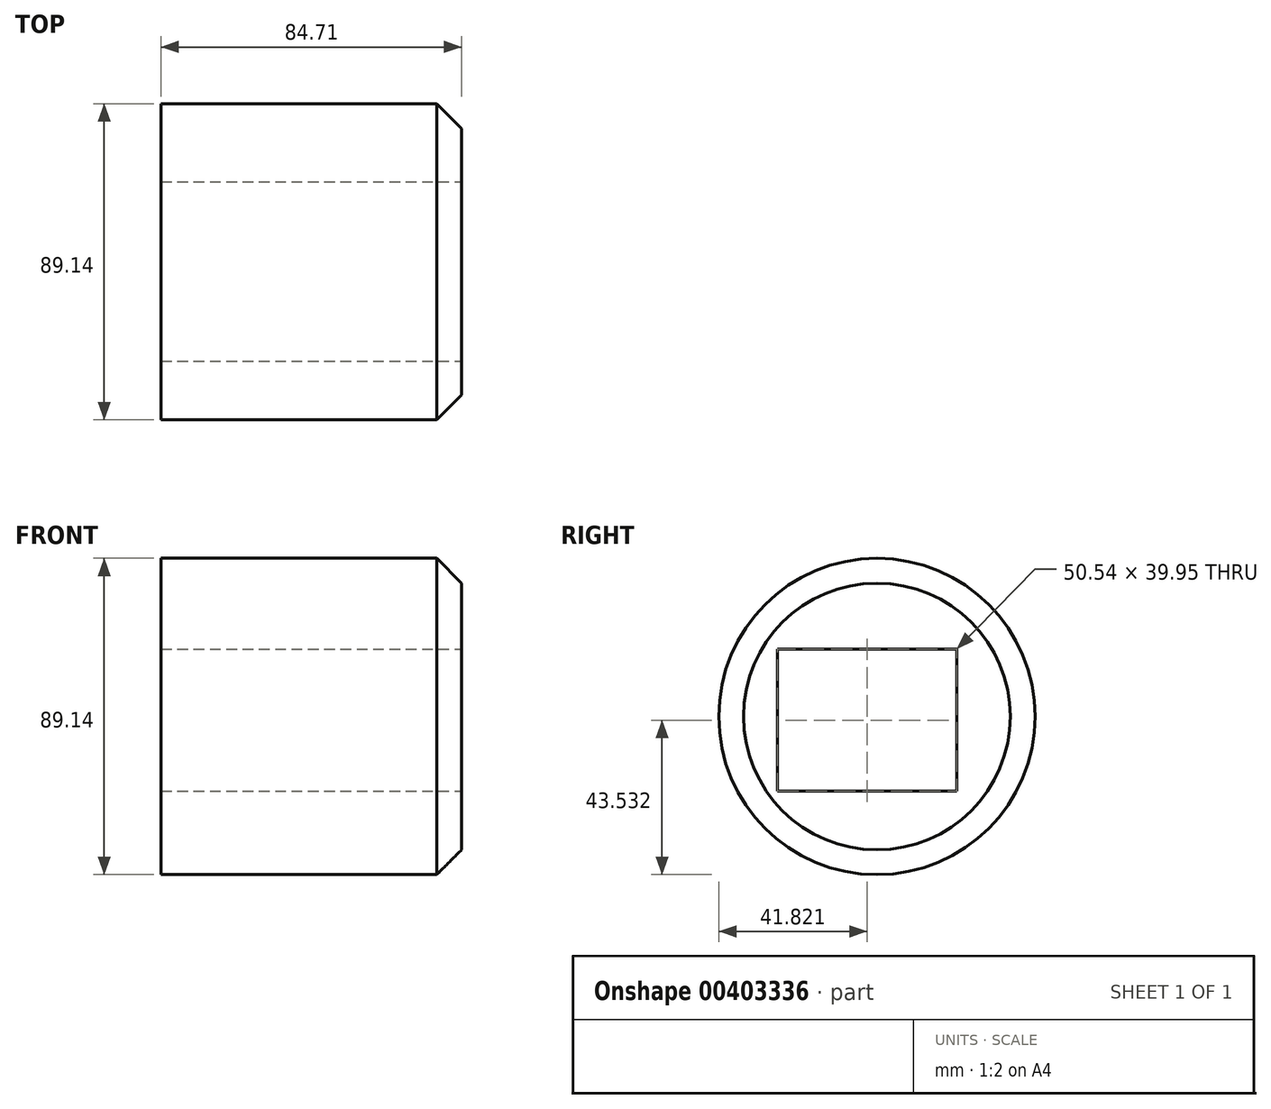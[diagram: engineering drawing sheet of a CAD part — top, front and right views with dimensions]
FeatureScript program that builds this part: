
annotation { "Feature Type Name" : "Feature", "Feature Type Description" : "" }
export const myFeature = defineFeature(function(context is Context, id is Id, definition is map)
    precondition{}
    {
        {
            var Q0;
            Q0=qCreatedBy(makeId("Right.planeOp"),FACE);
            var sketch = newSketch(context, id + "F0", { "sketchPlane" : qUnion([Q0])});
            skCircle(sketch, "E0", {"center": v(0, 0) * mm, "radius": 44.57 * mm});
            skSolve(sketch);
        }
        {
            var Q0;
            Q0=makeQuery(id+"F0.imprint","IMPRINT",FACE,{"disambiguationData":[TD([[makeQuery(id+"F0.imprint","IMPRINT",EDGE,{"derivedFrom":sQuery(id+"F0.wireOp",EDGE,"E0")}),1.0]])]});
            extrude(context, id + "F1", {"entities" : qUnion([Q0]), "depth" : 59.7 * mm});
        }
        {
            var Q0;
            Q0=makeQuery(id+"F1.opExtrude","CAP_FACE",FACE,{"disambiguationData":[OSD([sQuery(id+"F0.wireOp",EDGE,"E0")])],"isStart":false});
            extrude(context, id + "F2", {"entities" : qUnion([Q0]), "operationType" : NewBodyOperationType.ADD, "depth" : 25 * mm});
        }
        {
            var Q0;
            Q0=makeQuery(id+"F2.opExtrude","CAP_FACE",FACE,{"disambiguationData":[OSD([sQuery(id+"F0.wireOp",EDGE,"E0")])],"isStart":false});
            var sketch = newSketch(context, id + "F3", { "sketchPlane" : qUnion([Q0])});
            skLineSegment(sketch, "E1.bottom", {"start": v(22.52, 18.94) * mm, "end": v(-28.02, 18.94) * mm});
            skLineSegment(sketch, "E1.top", {"start": v(22.52, -21.01) * mm, "end": v(-28.02, -21.01) * mm});
            skLineSegment(sketch, "E1.left", {"start": v(22.52, 18.94) * mm, "end": v(22.52, -21.01) * mm});
            skLineSegment(sketch, "E1.right", {"start": v(-28.02, 18.94) * mm, "end": v(-28.02, -21.01) * mm});
            skSolve(sketch);
        }
        {
            var Q0;
            Q0 = qSketchRegion(id + "F3", true);
            extrude(context, id + "F4", {"entities" : qUnion([Q0]), "operationType" : NewBodyOperationType.REMOVE, "oppositeDirection" : true, "depth" : 128.1 * mm});
        }
        {
            var Q0;
            Q0=makeQuery(id+"F2.opExtrude","CAP_EDGE",EDGE,{"disambiguationData":[OSD([sQuery(id+"F0.wireOp",EDGE,"E0")])],"isStart":false});
            chamfer(context, id + "F5", {"entities" : qUnion([Q0]), "width" : 7 * mm, "tangentPropagation" : true});
        }
    });
